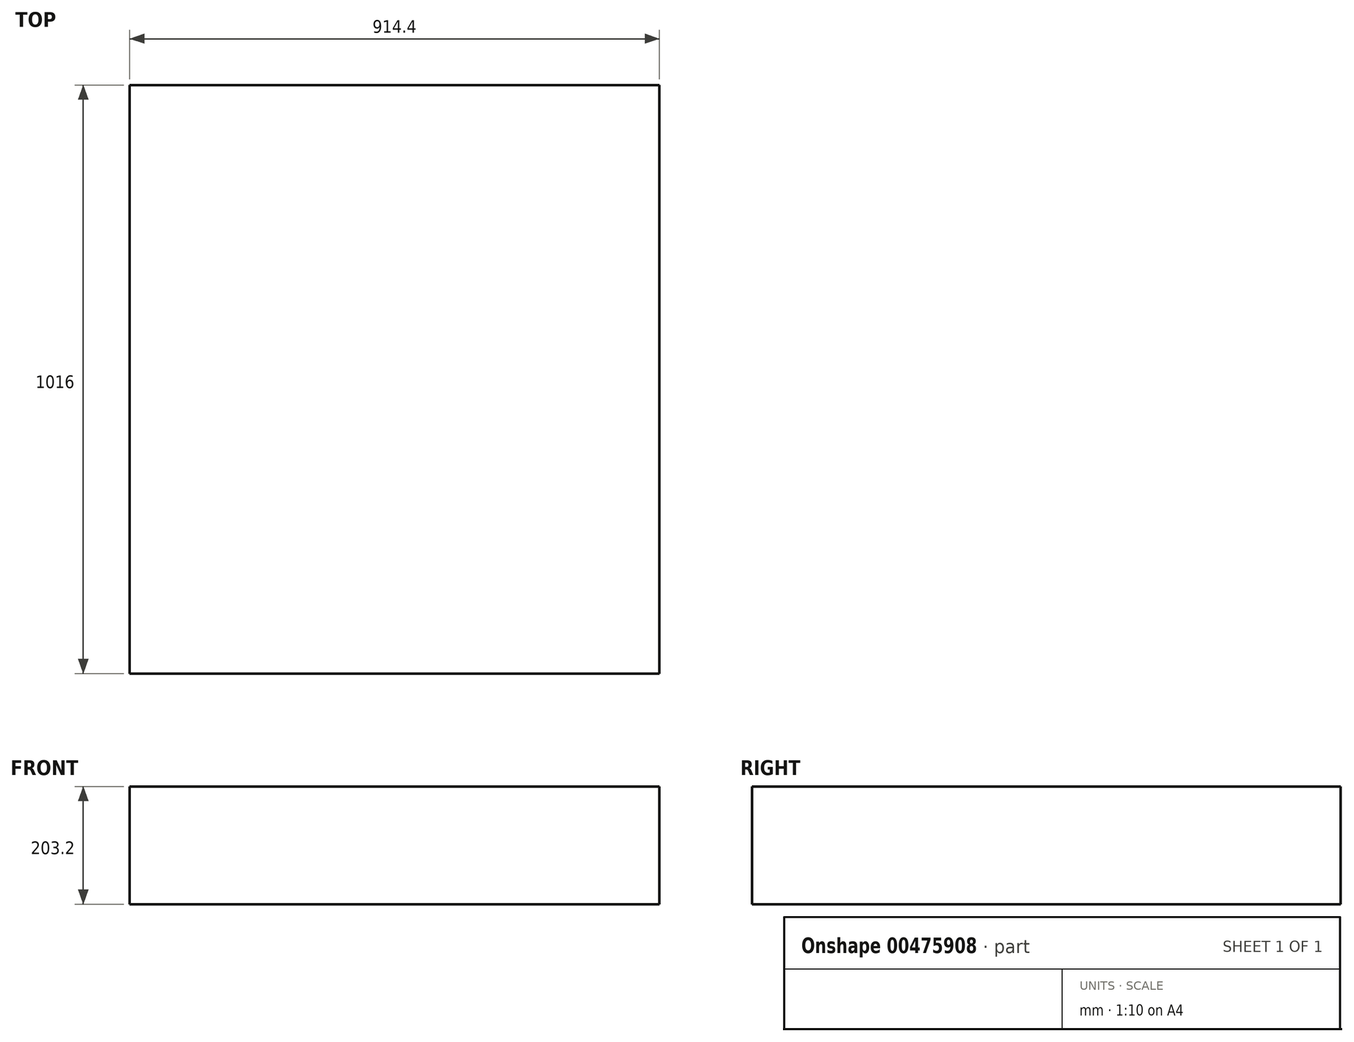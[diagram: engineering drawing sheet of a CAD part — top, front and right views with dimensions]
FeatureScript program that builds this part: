
annotation { "Feature Type Name" : "Feature", "Feature Type Description" : "" }
export const myFeature = defineFeature(function(context is Context, id is Id, definition is map)
    precondition{}
    {
        {
            var Q0;
            Q0=qCreatedBy(makeId("Front.planeOp"),FACE);
            var sketch = newSketch(context, id + "F0", { "sketchPlane" : qUnion([Q0])});
            skLineSegment(sketch, "E0.bottom", {"start": v(457.2, 101.6) * mm, "end": v(-457.2, 101.6) * mm});
            skLineSegment(sketch, "E0.top", {"start": v(457.2, -101.6) * mm, "end": v(-457.2, -101.6) * mm});
            skLineSegment(sketch, "E0.left", {"start": v(457.2, 101.6) * mm, "end": v(457.2, -101.6) * mm});
            skLineSegment(sketch, "E0.right", {"start": v(-457.2, 101.6) * mm, "end": v(-457.2, -101.6) * mm});
            skPoint(sketch, "E0.middle", {"position": v(0, 0) * mm});
            skSolve(sketch);
        }
        {
            var Q0;
            Q0=makeQuery(id+"F0.imprint","IMPRINT",FACE,{"disambiguationData":[TD([[makeQuery(id+"F0.imprint","IMPRINT",EDGE,{"derivedFrom":sQuery(id+"F0.wireOp",EDGE,"E0.bottom")}),1.0]])]});
            extrude(context, id + "F1", {"entities" : qUnion([Q0]), "endBound" : BoundingType.SYMMETRIC, "depth" : 1016 * mm, "offsetDistance" : 25.4 * mm});
        }
    });
